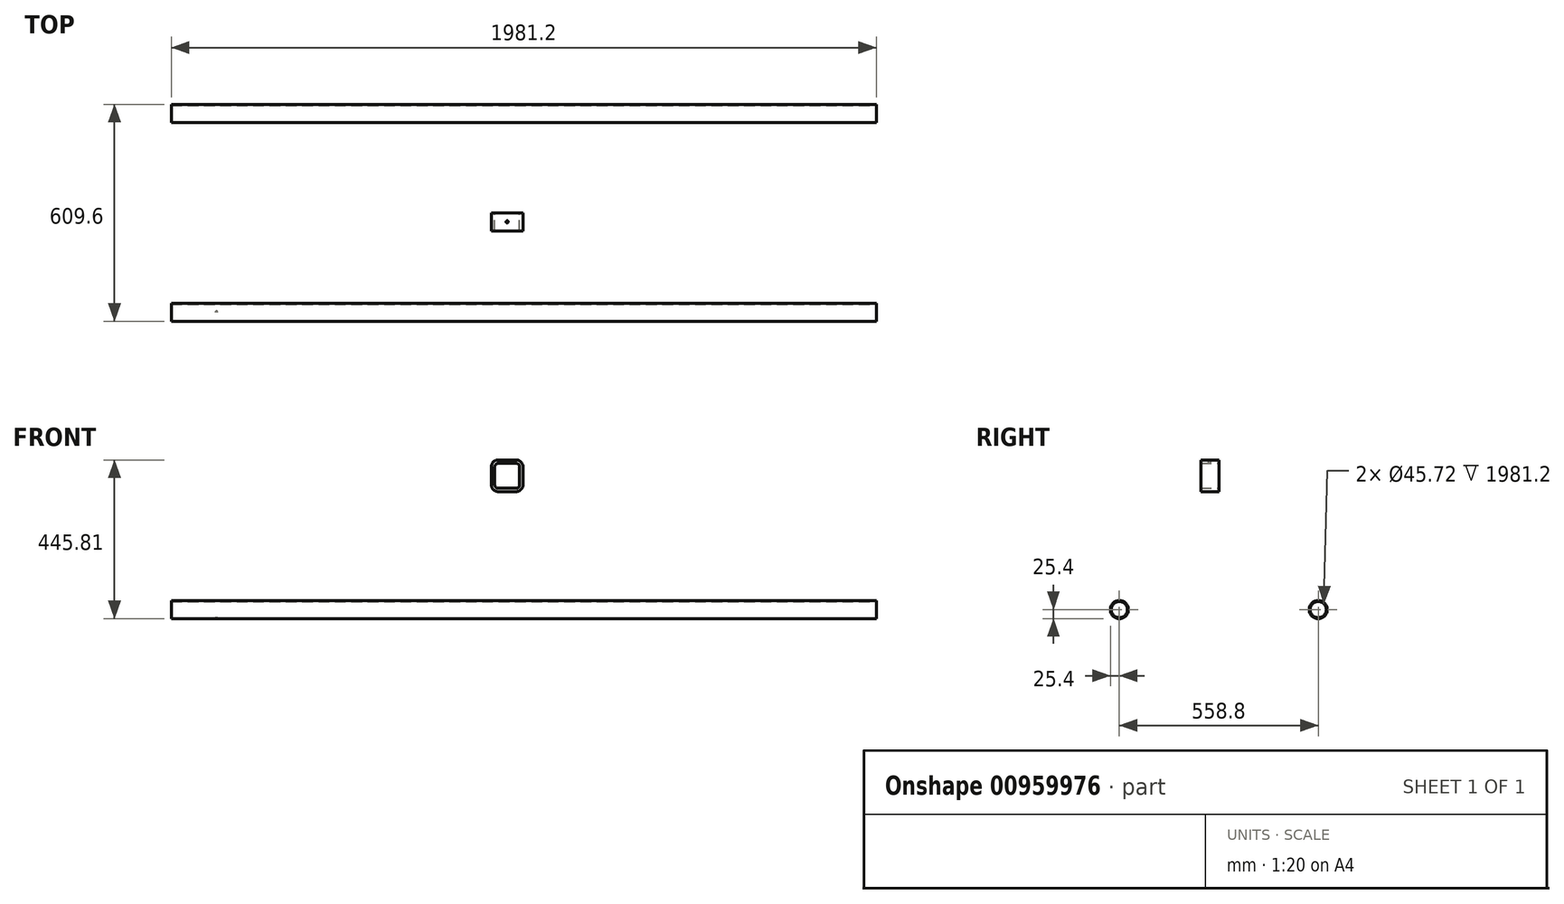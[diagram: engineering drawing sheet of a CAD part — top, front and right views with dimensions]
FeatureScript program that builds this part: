
annotation { "Feature Type Name" : "Feature", "Feature Type Description" : "" }
export const myFeature = defineFeature(function(context is Context, id is Id, definition is map)
    precondition{}
    {
        {
            var Q0;
            Q0=qCreatedBy(makeId("Right.planeOp"),FACE);
            var sketch = newSketch(context, id + "F0", { "sketchPlane" : qUnion([Q0])});
            skCircle(sketch, "E0", {"center": v(-279.4, 0) * mm, "radius": 25.4 * mm});
            skSolve(sketch);
        }
        {
            var Q0;
            Q0 = qSketchRegion(id + "F0", true);
            extrude(context, id + "F1", {"entities" : qUnion([Q0]), "oppositeDirection" : true, "depth" : 1981.2 * mm, "offsetDistance" : 25.4 * mm});
        }
        {
            var Q0;
            Q0=sQuery(id+"F0.wireOp",VERTEX,"E0.center");
            var Q1;
            Q1=makeQuery(id+"F1.opExtrude","SWEPT_BODY",BODY,{"disambiguationData":[OSD([sQuery(id+"F0.wireOp",EDGE,"E0")])]});
            hole(context, id + "F2", {"style" : HoleStyle.SIMPLE, "endStyle" : HoleEndStyle.THROUGH, "holeDiameter" : 45.72 * mm, "majorDiameter" : 6.35 * mm, "isTappedThrough" : true, "tappedDepth" : 12.7 * mm, "tapClearance" : 3, "locations" : qUnion([Q0]), "scope" : qUnion([Q1])});
        }
        {
            var Q0;
            Q0=qCreatedBy(makeId("Top.planeOp"),FACE);
            var sketch = newSketch(context, id + "F3", { "sketchPlane" : qUnion([Q0])});
            skCircle(sketch, "E1", {"center": v(-1854.2, -279.4) * mm, "radius": 3.18 * mm});
            skSolve(sketch);
        }
        {
            var Q0;
            Q0=sQuery(id+"F3.wireOp",VERTEX,"E1.center");
            var Q1;
            Q1=makeQuery(id+"F1.opExtrude","SWEPT_BODY",BODY,{"disambiguationData":[OSD([sQuery(id+"F0.wireOp",EDGE,"E0")])]});
            hole(context, id + "F4", {"style" : HoleStyle.SIMPLE, "endStyle" : HoleEndStyle.BLIND, "holeDiameter" : 6.35 * mm, "majorDiameter" : 6.35 * mm, "holeDepth" : 50.8 * mm, "isTappedThrough" : true, "tappedDepth" : 12.7 * mm, "tapClearance" : 3, "locations" : qUnion([Q0]), "scope" : qUnion([Q1])});
        }
        {
            var Q0;
            Q0=makeQuery(id+"F0.imprint","IMPRINT",FACE,{"disambiguationData":[TD([[makeQuery(id+"F0.imprint","IMPRINT",EDGE,{"derivedFrom":sQuery(id+"F0.wireOp",EDGE,"E0")}),1.0]])]});
            var sketch = newSketch(context, id + "F5", { "sketchPlane" : qUnion([Q0])});
            skCircle(sketch, "E2", {"center": v(279.4, 0) * mm, "radius": 25.4 * mm});
            skSolve(sketch);
        }
        {
            var Q0;
            Q0=makeQuery(id+"F5.imprint","IMPRINT",FACE,{"disambiguationData":[TD([[makeQuery(id+"F5.imprint","IMPRINT",EDGE,{"derivedFrom":sQuery(id+"F5.wireOp",EDGE,"E2")}),1.0]])]});
            var Q1;
            Q1=sQuery(id+"F5.wireOp",EDGE,"E2");
            extrude(context, id + "F6", {"entities" : qUnion([Q0]), "surfaceEntities" : qUnion([Q1]), "oppositeDirection" : true, "depth" : 1981.2 * mm, "offsetDistance" : 25.4 * mm});
        }
        {
            var Q0;
            Q0=sQuery(id+"F5.wireOp",VERTEX,"E2.center");
            var Q1;
            Q1=makeQuery(id+"F6.opExtrude","SWEPT_BODY",BODY,{"disambiguationData":[OSD([sQuery(id+"F5.wireOp",EDGE,"E2")])]});
            hole(context, id + "F7", {"style" : HoleStyle.SIMPLE, "endStyle" : HoleEndStyle.THROUGH, "holeDiameter" : 45.72 * mm, "majorDiameter" : 6.35 * mm, "isTappedThrough" : true, "tappedDepth" : 12.7 * mm, "tapClearance" : 3, "locations" : qUnion([Q0]), "scope" : qUnion([Q1])});
        }
        {
            var Q0;
            Q0=qCreatedBy(makeId("Front.planeOp"),FACE);
            var sketch = newSketch(context, id + "F8", { "sketchPlane" : qUnion([Q0])});
            skLineSegment(sketch, "E3.bottom", {"start": v(-1062.7, 420.4) * mm, "end": v(-1011.9, 420.4) * mm});
            skLineSegment(sketch, "E3.top", {"start": v(-1062.7, 331.5) * mm, "end": v(-1011.9, 331.5) * mm});
            skLineSegment(sketch, "E3.left", {"start": v(-1081.75, 401.36) * mm, "end": v(-1081.75, 350.56) * mm});
            skLineSegment(sketch, "E3.right", {"start": v(-992.85, 401.36) * mm, "end": v(-992.85, 350.56) * mm});
            skPoint(sketch, "E4.visualSharp", {"position": v(-1081.75, 420.4) * mm});
            skArc(sketch, "E4.filletArc", {"start": v(-1062.7, 420.4) * mm, "mid": v(-1076.17, 414.83) * mm, "end": v(-1081.75, 401.36) * mm});
            skPoint(sketch, "E5.visualSharp", {"position": v(-992.85, 420.4) * mm});
            skArc(sketch, "E5.filletArc", {"start": v(-992.85, 401.36) * mm, "mid": v(-998.43, 414.83) * mm, "end": v(-1011.9, 420.4) * mm});
            skPoint(sketch, "E6.visualSharp", {"position": v(-992.85, 331.5) * mm});
            skArc(sketch, "E6.filletArc", {"start": v(-1011.9, 331.5) * mm, "mid": v(-998.43, 337.09) * mm, "end": v(-992.85, 350.56) * mm});
            skPoint(sketch, "E7.visualSharp", {"position": v(-1081.75, 331.5) * mm});
            skArc(sketch, "E7.filletArc", {"start": v(-1081.75, 350.56) * mm, "mid": v(-1076.17, 337.09) * mm, "end": v(-1062.7, 331.5) * mm});
            skLineSegment(sketch, "E8.bottom", {"start": v(-25.4, 34.93) * mm, "end": v(25.4, 34.93) * mm});
            skLineSegment(sketch, "E8.top", {"start": v(-25.4, -34.92) * mm, "end": v(25.4, -34.92) * mm});
            skLineSegment(sketch, "E8.left", {"start": v(-34.92, 25.4) * mm, "end": v(-34.92, -25.4) * mm});
            skLineSegment(sketch, "E8.right", {"start": v(34.93, 25.4) * mm, "end": v(34.93, -25.4) * mm});
            skPoint(sketch, "E9.visualSharp", {"position": v(-34.92, -34.92) * mm});
            skArc(sketch, "E9.filletArc", {"start": v(-34.92, -25.4) * mm, "mid": v(-32.14, -32.14) * mm, "end": v(-25.4, -34.92) * mm});
            skPoint(sketch, "E10.visualSharp", {"position": v(-34.92, 34.93) * mm});
            skArc(sketch, "E10.filletArc", {"start": v(-25.4, 34.93) * mm, "mid": v(-32.14, 32.14) * mm, "end": v(-34.92, 25.4) * mm});
            skPoint(sketch, "E11.visualSharp", {"position": v(34.93, 34.93) * mm});
            skArc(sketch, "E11.filletArc", {"start": v(34.93, 25.4) * mm, "mid": v(32.14, 32.14) * mm, "end": v(25.4, 34.93) * mm});
            skPoint(sketch, "E12.visualSharp", {"position": v(34.93, -34.92) * mm});
            skArc(sketch, "E12.filletArc", {"start": v(25.4, -34.92) * mm, "mid": v(32.14, -32.14) * mm, "end": v(34.93, -25.4) * mm});
            skLineSegment(sketch, "E13.bottom", {"start": v(-1062.7, 410.88) * mm, "end": v(-1011.9, 410.88) * mm});
            skLineSegment(sketch, "E13.top", {"start": v(-1062.7, 341.03) * mm, "end": v(-1011.9, 341.03) * mm});
            skLineSegment(sketch, "E13.left", {"start": v(-1072.23, 401.36) * mm, "end": v(-1072.23, 350.56) * mm});
            skLineSegment(sketch, "E13.right", {"start": v(-1002.38, 401.36) * mm, "end": v(-1002.38, 350.56) * mm});
            skPoint(sketch, "E14.visualSharp", {"position": v(-1072.23, 341.03) * mm});
            skArc(sketch, "E14.filletArc", {"start": v(-1072.23, 350.56) * mm, "mid": v(-1069.44, 343.82) * mm, "end": v(-1062.7, 341.03) * mm});
            skPoint(sketch, "E15.visualSharp", {"position": v(-1072.23, 410.88) * mm});
            skArc(sketch, "E15.filletArc", {"start": v(-1062.7, 410.88) * mm, "mid": v(-1069.44, 408.1) * mm, "end": v(-1072.23, 401.36) * mm});
            skPoint(sketch, "E16.visualSharp", {"position": v(-1002.38, 410.88) * mm});
            skArc(sketch, "E16.filletArc", {"start": v(-1002.38, 401.36) * mm, "mid": v(-1005.17, 408.1) * mm, "end": v(-1011.9, 410.88) * mm});
            skPoint(sketch, "E17.visualSharp", {"position": v(-1002.38, 341.03) * mm});
            skArc(sketch, "E17.filletArc", {"start": v(-1011.9, 341.03) * mm, "mid": v(-1005.17, 343.82) * mm, "end": v(-1002.38, 350.56) * mm});
            skSolve(sketch);
        }
        {
            var Q0;
            Q0=makeQuery(id+"F8.imprint","IMPRINT",FACE,{"disambiguationData":[TD([[makeQuery(id+"F8.imprint","IMPRINT",EDGE,{"derivedFrom":sQuery(id+"F8.wireOp",EDGE,"E3.bottom")}),-1.0]])]});
            extrude(context, id + "F9", {"entities" : qUnion([Q0]), "depth" : 50.8 * mm, "offsetDistance" : 25.4 * mm});
        }
        {
            var Q0;
            Q0=makeQuery(id+"F9.opExtrude","SWEPT_FACE",FACE,{"disambiguationData":[OSD([sQuery(id+"F8.wireOp",EDGE,"E3.bottom")])]});
            var sketch = newSketch(context, id + "F10", { "sketchPlane" : qUnion([Q0])});
            skCircle(sketch, "E18", {"center": v(-1037.3, -25.4) * mm, "radius": 3.18 * mm});
            skSolve(sketch);
        }
        {
            var Q0;
            Q0=sQuery(id+"F10.wireOp",VERTEX,"E18.center");
            var Q1;
            Q1=makeQuery(id+"F9.opExtrude","SWEPT_BODY",BODY,{"disambiguationData":[OSD([sQuery(id+"F8.wireOp",EDGE,"E3.bottom"),sQuery(id+"F8.wireOp",EDGE,"E3.top"),sQuery(id+"F8.wireOp",EDGE,"E3.left"),sQuery(id+"F8.wireOp",EDGE,"E3.right"),sQuery(id+"F8.wireOp",EDGE,"E4.filletArc"),sQuery(id+"F8.wireOp",EDGE,"E5.filletArc"),sQuery(id+"F8.wireOp",EDGE,"E6.filletArc"),sQuery(id+"F8.wireOp",EDGE,"E7.filletArc"),sQuery(id+"F8.wireOp",EDGE,"E13.bottom"),sQuery(id+"F8.wireOp",EDGE,"E13.top"),sQuery(id+"F8.wireOp",EDGE,"E13.left"),sQuery(id+"F8.wireOp",EDGE,"E13.right"),sQuery(id+"F8.wireOp",EDGE,"E14.filletArc"),sQuery(id+"F8.wireOp",EDGE,"E15.filletArc"),sQuery(id+"F8.wireOp",EDGE,"E16.filletArc"),sQuery(id+"F8.wireOp",EDGE,"E17.filletArc")])]});
            hole(context, id + "F11", {"style" : HoleStyle.SIMPLE, "endStyle" : HoleEndStyle.BLIND, "holeDiameter" : 6.35 * mm, "majorDiameter" : 6.35 * mm, "holeDepth" : 12.7 * mm, "isTappedThrough" : true, "tappedDepth" : 12.7 * mm, "tapClearance" : 3, "locations" : qUnion([Q0]), "scope" : qUnion([Q1])});
        }
    });
